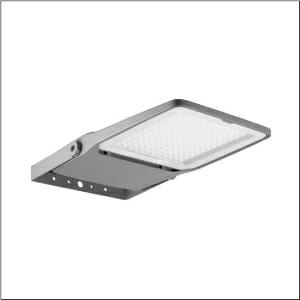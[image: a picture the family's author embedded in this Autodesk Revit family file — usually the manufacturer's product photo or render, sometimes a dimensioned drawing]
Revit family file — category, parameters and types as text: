
# Revit family: floodlight_fl_20_midi___pl52_5xa7682d1d2ac_d798
name_source: partatom
category: Lighting Fixtures
units: mm (PartAtom-declared; Revit-internal decimal feet)

## family parameters
Cut with Voids When Loaded = No
Host = Face
Light Source = No
Part Type = Normal
Room Calculation Point = No
Round Connector Dimension = Use Diameter
Shared = No

## types (1)
- --- (1 x LED 3000K / CRI = 80 (unbekannt), 14130 lm, 3000K)
    Apparent Load = 142 VA
    CIE Flux Codes = 27 59 98 100 100
    Color Rendering = 80
    Color Temperature = 3000K
    Default Elevation = 1800 mm
    Description = Floodlight FL 20 midi, floodlight, primary light control with lens, of plastic, primary optical cover: protective disc, of toughened safety glass, transparent, light distribution: PL52, light emission: direct distribution, primary light characteristic: asymmetric, installation type: surface-mounted, LED, High Power LED, rated luminous flux: 14.130lm, luminous efficacy: 100lm/W, light colour: 830, colour temperature: 3000K, control gear: ECG Plus, control: flexible luminous flux parameterisation, time-dependent luminous flux control, digital communication interface, power reduction, overheat protection, electronic power reduction, with terminal, 5-pole, max. 2.5mm², mains connection: 220..240V, AC, 50/60Hz, rated input power: 142W, LED unit, of diecast aluminium, powder-coated, Siteco® metallic grey (DB 702S), corrosivity category C5 mid according to DIN EN ISO 12944, incl. 1x M20 cable gland for cable Ø 6.5..12mm, length: 731mm, width: 450mm, height: 76mm, housing frame, of diecast aluminium, powder-coated, Siteco® metallic grey (DB 702S), wall fastening, of steel, powder-coated, Siteco® metallic grey (DB 702S), DALI, protection rating (complete): IP66, insulation class (complete): insulation class II (safety insulation), certification: CE, ENEC, VDE, protection symbol: D, permissible operating ambient temperature: -40..+40°C, permissible operating ambient temperature for outdoor applications: -40..+50°C, standard: DIN EN 12944, packaging unit: 1 piece

Light Distribution: PL52
    Height = 76 mm
    Lamp = 1 x LED 3000K / CRI >= 80 (unbekannt)
    Lamp Light Flux = 14130 lm
    Lamp count = 1
    Length = 731 mm
    Luminous efficacy = 100 lm/W
    Manufacturer = Siteco
    ModVariant = No
    Model = 5XA7682D1D2AC
    Mounting Place = Wall
    Mounting Type = Surface mounted
    Number of Poles = 1
    OnlyDefault = Yes
    Power Factor = 1
    Product Name = Floodlight FL 20 midi | PL52
    Product group = floodlight | wall mounted
    ProductGroupID = 2001
    Protection Class = Protection class II
    Protection Degree = IP 66
    RLX_Detail_Level = 1
    RLX_Emergency_Light_Flux = 0 lm
    RLX_Emergency_Type = 0
    RLX_Emergency_Type_DB = No
    RlxData = <blob elided: 92213 chars, md5=dc1c4cc8>
    Socket = socket
    Standby Power = 0 W
    System Light Flux = 14130 lm
    System Power = 142 W
    Type Comments = factory setting: luminous flux: 100 % | dim-lin: 254 | 489 mA
    Type Image = l_1005944.jpg
    URL = http://relux.com
    VarID = @adj_148005
    Voltage = 0 V
    Weight = 0.00 kg
    Width = 450 mm

## geometry (parser evidence)
native form markers: Blend x4, Sweep x13
no freeform markers — native parametric forms only
